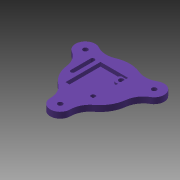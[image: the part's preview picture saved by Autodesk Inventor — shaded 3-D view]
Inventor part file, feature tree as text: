
AUTODESK INVENTOR PART (.ipt)
format: ipt  version: 2014 (Build 180170000, 170)  size: 162,816 bytes
history: native  units: in
note: dims shown in document units (in); Inventor stores cm internally (conversion verified against a paired STEP export)
features: extrude x6, sketch x6, pattern_circular x1
ambient origin geometry x8: Origin, YZ Plane, XZ Plane, XY Plane, X Axis, Y Axis, Z Axis, Center Point
bodies: Solid1 (feature_tree)
feature tree (13):
  extrude  "Extrusion1"  Depth=1.0in
  extrude  "Extrusion2"  Depth=0.15in TaperAngle=0.0deg
  pattern_circular  "Circular Pattern1"  Count=3 Angle=360.0deg
  extrude  "Extrusion3"  Depth=0.695in
  extrude  "Extrusion4"  Depth=0.1in TaperAngle=0.0deg
  extrude  "Extrusion5"  Depth=0.25in
  extrude  "Extrusion6"  Depth=0.25in
  sketch  "Sketch1"  dims[d0=1.0in d1=1.5in]
  sketch  "Sketch2"  dims[d2=0.5in d3=0.15in d4=0.0in]
  sketch  "Sketch3"  dims[d5=0.12in]
  sketch  "Sketch4"  dims[d6=0.2in d7=0.0in d8=1.1811in d9=360.0deg]
  sketch  "Sketch5"  dims[d11=0.88in d12=0.695in]
  sketch  "Sketch6"  dims[d14=0.4185in d15=0.1in d16=0.0in d17=0.12in d18=0.087in d19=0.087in d20=0.087in d21=0.1in d22=0.0in d23=0.05in d24=0.0in d25=0.1in d26=0.1in d27=0.05in d28=0.0in d29=0.291in d30=0.5in d31=0.25in]
